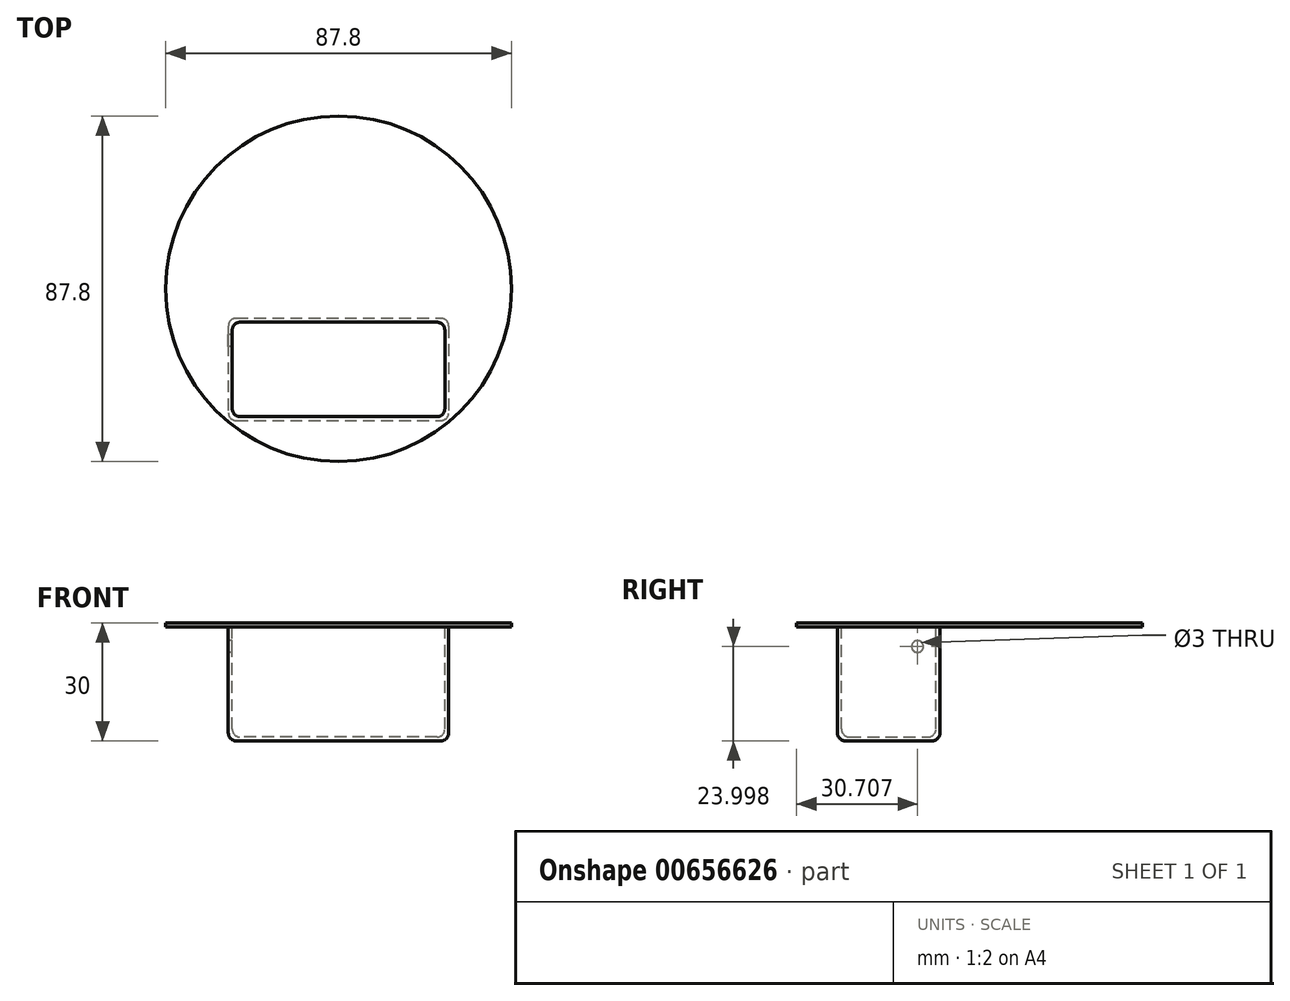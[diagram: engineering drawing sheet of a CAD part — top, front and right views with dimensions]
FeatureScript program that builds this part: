
annotation { "Feature Type Name" : "Feature", "Feature Type Description" : "" }
export const myFeature = defineFeature(function(context is Context, id is Id, definition is map)
    precondition{}
    {
        {
            var Q0;
            Q0=qCreatedBy(makeId("Front.planeOp"),FACE);
            var sketch = newSketch(context, id + "F0", { "sketchPlane" : qUnion([Q0])});
            skPoint(sketch, "E0.orphan", {"position": v(0, -3.82) * mm});
            skPoint(sketch, "E1.start.orphan", {"position": v(0, -5) * mm});
            skLineSegment(sketch, "E2", {"start": v(0, -3.82) * mm, "end": v(0, -5) * mm});
            skPoint(sketch, "E3.visualSharp", {"position": v(-43.9, -20.26) * mm});
            skLineSegment(sketch, "E4", {"start": v(-43.9, -20.26) * mm, "end": v(0, -20.26) * mm});
            skLineSegment(sketch, "E5", {"start": v(-43.9, -19.26) * mm, "end": v(0, -19.26) * mm});
            skLineSegment(sketch, "E6", {"start": v(0, -19.26) * mm, "end": v(0, -20.26) * mm});
            skLineSegment(sketch, "E7", {"start": v(-43.9, -19.26) * mm, "end": v(-43.9, -20.26) * mm});
            skSolve(sketch);
        }
        {
            var Q0;
            Q0=makeQuery(id+"F0.imprint","IMPRINT",FACE,{"disambiguationData":[TD([[makeQuery(id+"F0.imprint","IMPRINT",EDGE,{"derivedFrom":sQuery(id+"F0.wireOp",EDGE,"E4")}),1.0]])]});
            var Q1;
            Q1=sQuery(id+"F0.wireOp",EDGE,"E2");
            revolve(context, id + "F1", {"surfaceOperationType" : NewSurfaceOperationType.NEW, "entities" : qUnion([Q0]), "axis" : qUnion([Q1]), "revolveType" : RevolveType.FULL});
        }
        {
            var Q0;
            Q0=makeQuery(id+"F1.opRevolve","SWEPT_FACE",FACE,{"disambiguationData":[OSD([sQuery(id+"F0.wireOp",EDGE,"E5")])]});
            var sketch = newSketch(context, id + "F2", { "sketchPlane" : qUnion([Q0])});
            skLineSegment(sketch, "E8", {"start": v(0, 0) * mm, "end": v(0, -41) * mm, "construction": true});
            skLineSegment(sketch, "E9.bottom", {"start": v(26, -33.5) * mm, "end": v(-26, -33.5) * mm});
            skLineSegment(sketch, "E9.top", {"start": v(26, -7.5) * mm, "end": v(-26, -7.5) * mm});
            skLineSegment(sketch, "E9.left", {"start": v(28, -31.5) * mm, "end": v(28, -9.5) * mm});
            skLineSegment(sketch, "E9.right", {"start": v(-28, -31.5) * mm, "end": v(-28, -9.5) * mm});
            skPoint(sketch, "E9.middle", {"position": v(0, -20.5) * mm});
            skLineSegment(sketch, "E10.0", {"start": v(25, -8.5) * mm, "end": v(-25, -8.5) * mm});
            skLineSegment(sketch, "E10.1", {"start": v(27, -30.5) * mm, "end": v(27, -10.5) * mm});
            skLineSegment(sketch, "E10.2", {"start": v(25, -32.5) * mm, "end": v(-25, -32.5) * mm});
            skLineSegment(sketch, "E10.3", {"start": v(-27, -30.5) * mm, "end": v(-27, -10.5) * mm});
            skPoint(sketch, "E11.visualSharp", {"position": v(28, -7.5) * mm});
            skArc(sketch, "E11.filletArc", {"start": v(28, -9.5) * mm, "mid": v(27.41, -8.09) * mm, "end": v(26, -7.5) * mm});
            skPoint(sketch, "E12.visualSharp", {"position": v(27, -8.5) * mm});
            skArc(sketch, "E12.filletArc", {"start": v(27, -10.5) * mm, "mid": v(26.41, -9.09) * mm, "end": v(25, -8.5) * mm});
            skPoint(sketch, "E13.visualSharp", {"position": v(-27, -8.5) * mm});
            skArc(sketch, "E13.filletArc", {"start": v(-25, -8.5) * mm, "mid": v(-26.41, -9.09) * mm, "end": v(-27, -10.5) * mm});
            skPoint(sketch, "E14.visualSharp", {"position": v(-28, -7.5) * mm});
            skArc(sketch, "E14.filletArc", {"start": v(-26, -7.5) * mm, "mid": v(-27.41, -8.09) * mm, "end": v(-28, -9.5) * mm});
            skPoint(sketch, "E15.visualSharp", {"position": v(-28, -33.5) * mm});
            skArc(sketch, "E15.filletArc", {"start": v(-28, -31.5) * mm, "mid": v(-27.41, -32.91) * mm, "end": v(-26, -33.5) * mm});
            skPoint(sketch, "E16.visualSharp", {"position": v(-27, -32.5) * mm});
            skArc(sketch, "E16.filletArc", {"start": v(-27, -30.5) * mm, "mid": v(-26.41, -31.91) * mm, "end": v(-25, -32.5) * mm});
            skPoint(sketch, "E17.visualSharp", {"position": v(27, -32.5) * mm});
            skArc(sketch, "E17.filletArc", {"start": v(25, -32.5) * mm, "mid": v(26.41, -31.91) * mm, "end": v(27, -30.5) * mm});
            skPoint(sketch, "E18.visualSharp", {"position": v(28, -33.5) * mm});
            skArc(sketch, "E18.filletArc", {"start": v(26, -33.5) * mm, "mid": v(27.41, -32.91) * mm, "end": v(28, -31.5) * mm});
            skSolve(sketch);
        }
        {
            var Q0;
            Q0=makeQuery(id+"F2.imprint","IMPRINT",FACE,{"disambiguationData":[TD([[makeQuery(id+"F2.imprint","IMPRINT",EDGE,{"derivedFrom":sQuery(id+"F2.wireOp",EDGE,"E10.0")}),1.0]])]});
            var Q1;
            Q1=makeQuery(id+"F2.imprint","IMPRINT",FACE,{"disambiguationData":[TD([[makeQuery(id+"F2.imprint","IMPRINT",EDGE,{"derivedFrom":sQuery(id+"F2.wireOp",EDGE,"E9.bottom")}),-1.0]])]});
            extrude(context, id + "F3", {"entities" : qUnion([Q0, Q1]), "operationType" : NewBodyOperationType.ADD, "oppositeDirection" : true, "depth" : 30 * mm, "offsetDistance" : 25 * mm});
        }
        {
            var Q0;
            Q0=makeQuery(id+"F2.imprint","IMPRINT",FACE,{"disambiguationData":[TD([[makeQuery(id+"F2.imprint","IMPRINT",EDGE,{"derivedFrom":sQuery(id+"F2.wireOp",EDGE,"E10.0")}),1.0]])]});
            extrude(context, id + "F4", {"entities" : qUnion([Q0]), "operationType" : NewBodyOperationType.REMOVE, "oppositeDirection" : true, "depth" : 29 * mm, "offsetDistance" : 25 * mm});
        }
        {
            var Q0;
            Q0=makeQuery(id+"F3.opExtrude","CAP_FACE",FACE,{"disambiguationData":[OSD([sQuery(id+"F2.wireOp",EDGE,"E9.bottom"),sQuery(id+"F2.wireOp",EDGE,"E9.top"),sQuery(id+"F2.wireOp",EDGE,"E9.left"),sQuery(id+"F2.wireOp",EDGE,"E9.right"),sQuery(id+"F2.wireOp",EDGE,"E11.filletArc"),sQuery(id+"F2.wireOp",EDGE,"E14.filletArc"),sQuery(id+"F2.wireOp",EDGE,"E15.filletArc"),sQuery(id+"F2.wireOp",EDGE,"E18.filletArc")])],"isStart":false});
            var Q1;
            Q1=makeQuery(id+"F4.boolean.opBoolean","COPY",FACE,{"derivedFrom":makeQuery(id+"F4.opExtrude","CAP_FACE",FACE,{"disambiguationData":[OSD([sQuery(id+"F2.wireOp",EDGE,"E10.0"),sQuery(id+"F2.wireOp",EDGE,"E10.1"),sQuery(id+"F2.wireOp",EDGE,"E10.2"),sQuery(id+"F2.wireOp",EDGE,"E10.3"),sQuery(id+"F2.wireOp",EDGE,"E12.filletArc"),sQuery(id+"F2.wireOp",EDGE,"E13.filletArc"),sQuery(id+"F2.wireOp",EDGE,"E16.filletArc"),sQuery(id+"F2.wireOp",EDGE,"E17.filletArc")])],"isStart":false})});
            fillet(context, id + "F5", {"entities" : qUnion([Q0, Q1]), "radius" : 2 * mm, "tangentPropagation" : true, "defaultsChanged" : false, "vertexSettings" : [], "allowEdgeOverflow" : false});
        }
        {
            var Q0;
            Q0=makeQuery(id+"F3.opExtrude","SWEPT_FACE",FACE,{"disambiguationData":[OSD([sQuery(id+"F2.wireOp",EDGE,"E9.right")])]});
            var sketch = newSketch(context, id + "F6", { "sketchPlane" : qUnion([Q0])});
            skCircle(sketch, "E19", {"center": v(13.2, -25.26) * mm, "radius": 1.5 * mm});
            skSolve(sketch);
        }
        {
            var Q0;
            Q0=makeQuery(id+"F6.imprint","IMPRINT",FACE,{"disambiguationData":[TD([[makeQuery(id+"F6.imprint","IMPRINT",EDGE,{"derivedFrom":sQuery(id+"F6.wireOp",EDGE,"E19")}),1.0]])]});
            extrude(context, id + "F7", {"entities" : qUnion([Q0]), "operationType" : NewBodyOperationType.REMOVE, "oppositeDirection" : true, "depth" : 4.7 * mm, "offsetDistance" : 25 * mm});
        }
    });
